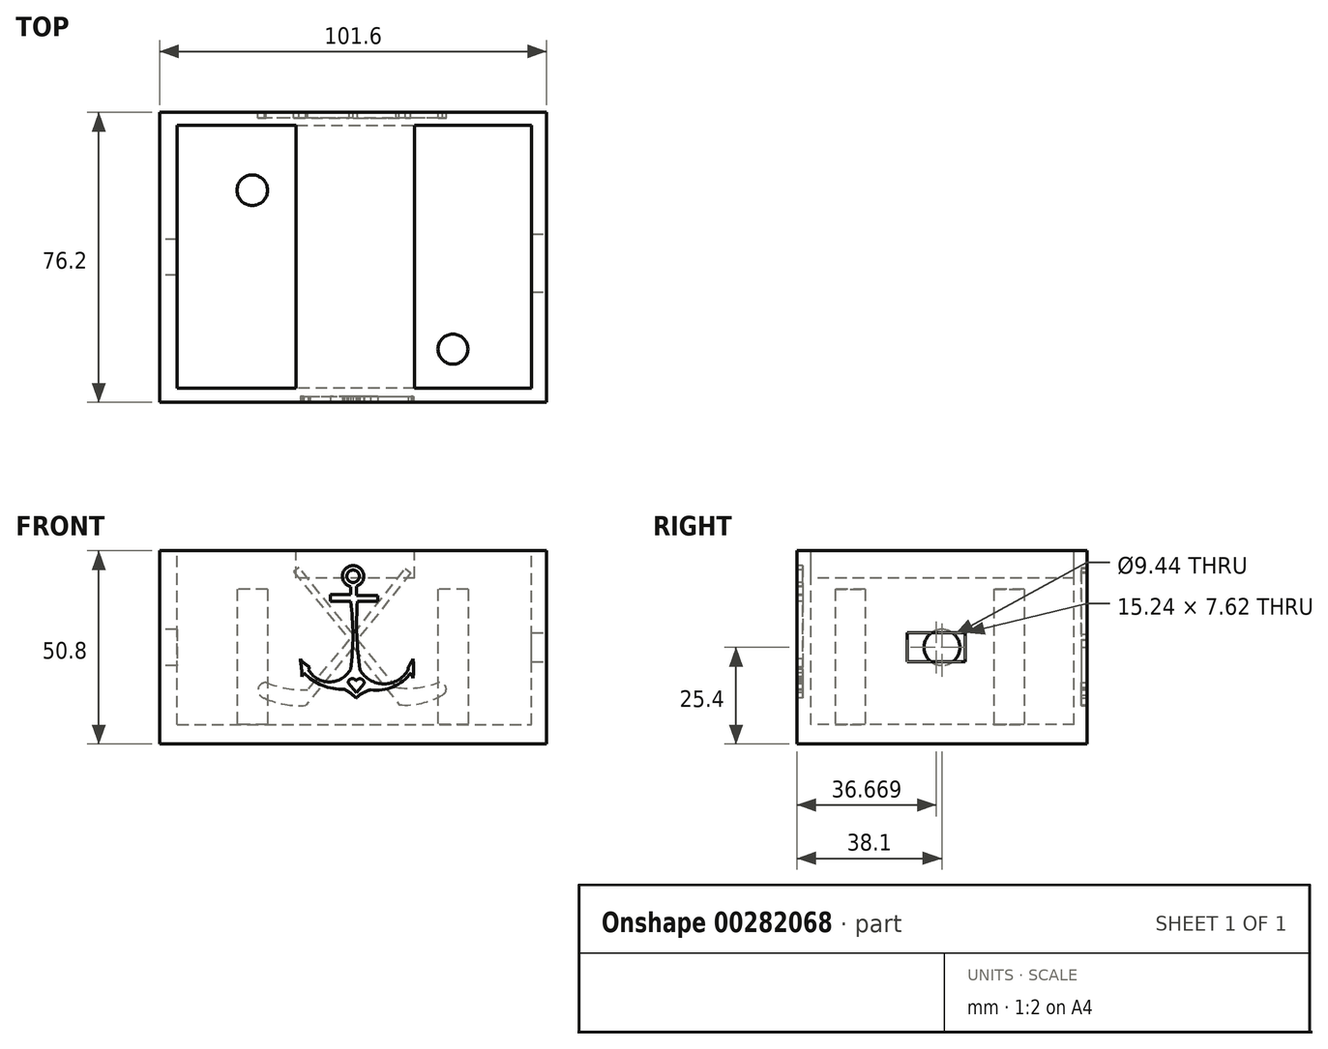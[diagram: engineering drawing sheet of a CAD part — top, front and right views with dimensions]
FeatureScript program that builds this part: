
annotation { "Feature Type Name" : "Feature", "Feature Type Description" : "" }
export const myFeature = defineFeature(function(context is Context, id is Id, definition is map)
    precondition{}
    {
        {
            var Q0;
            Q0=qCreatedBy(makeId("Front.planeOp"),FACE);
            var sketch = newSketch(context, id + "F0", { "sketchPlane" : qUnion([Q0])});
            skLineSegment(sketch, "E0.bottom", {"start": v(-50.8, 25.4) * mm, "end": v(50.8, 25.4) * mm});
            skLineSegment(sketch, "E0.top", {"start": v(-50.8, -25.4) * mm, "end": v(50.8, -25.4) * mm});
            skLineSegment(sketch, "E0.left", {"start": v(-50.8, 25.4) * mm, "end": v(-50.8, -25.4) * mm});
            skLineSegment(sketch, "E0.right", {"start": v(50.8, 25.4) * mm, "end": v(50.8, -25.4) * mm});
            skPoint(sketch, "E0.middle", {"position": v(0, 0) * mm});
            skSolve(sketch);
        }
        {
            var Q0;
            Q0=makeQuery(id+"F0.imprint","IMPRINT",FACE,{"disambiguationData":[TD([[makeQuery(id+"F0.imprint","IMPRINT",EDGE,{"derivedFrom":sQuery(id+"F0.wireOp",EDGE,"E0.bottom")}),-1.0]])]});
            extrude(context, id + "F1", {"entities" : qUnion([Q0]), "oppositeDirection" : true, "depth" : 76.2 * mm});
        }
        {
            var Q0;
            Q0=makeQuery(id+"F1.opExtrude","SWEPT_FACE",FACE,{"disambiguationData":[OSD([sQuery(id+"F0.wireOp",EDGE,"E0.bottom")])]});
            var sketch = newSketch(context, id + "F2", { "sketchPlane" : qUnion([Q0])});
            skLineSegment(sketch, "E1.bottom", {"start": v(-46.23, 72.86) * mm, "end": v(-14.92, 72.86) * mm});
            skLineSegment(sketch, "E1.top", {"start": v(-46.23, 3.7) * mm, "end": v(-14.92, 3.7) * mm});
            skLineSegment(sketch, "E1.left", {"start": v(-46.23, 72.86) * mm, "end": v(-46.23, 3.7) * mm});
            skLineSegment(sketch, "E1.right", {"start": v(46.93, 72.86) * mm, "end": v(46.93, 3.7) * mm});
            skLineSegment(sketch, "E2.bottom", {"start": v(16.2, 76.2) * mm, "end": v(-14.92, 76.2) * mm});
            skLineSegment(sketch, "E2.top", {"start": v(16.2, 0) * mm, "end": v(-14.92, 0) * mm});
            skLineSegment(sketch, "E2.left", {"start": v(16.2, 76.2) * mm, "end": v(16.2, 0) * mm});
            skLineSegment(sketch, "E2.right", {"start": v(-14.92, 76.2) * mm, "end": v(-14.92, 0) * mm});
            skLineSegment(sketch, "E3.trimOffspring", {"start": v(16.2, 72.86) * mm, "end": v(46.93, 72.86) * mm});
            skLineSegment(sketch, "E4.trimOffspring", {"start": v(16.2, 3.7) * mm, "end": v(46.93, 3.7) * mm});
            skSolve(sketch);
        }
        {
            var Q0;
            {var subQ0=sQuery(id+"F2.wireOp",EDGE,"E1.bottom");Q0=makeQuery(id+"F2.imprint","IMPRINT",FACE,{"disambiguationData":[TD([[makeQuery(id+"F2.imprint","IMPRINT",EDGE,{"derivedFrom":subQ0}),-1.0]])]});}
            var Q1;
            Q1=makeQuery(id+"F2.imprint","IMPRINT",FACE,{"disambiguationData":[TD([[makeQuery(id+"F2.imprint","IMPRINT",EDGE,{"derivedFrom":sQuery(id+"F2.wireOp",EDGE,"E1.right")}),-1.0]])]});
            extrude(context, id + "F3", {"entities" : qUnion([Q0, Q1]), "operationType" : NewBodyOperationType.REMOVE, "oppositeDirection" : true, "depth" : 45.72 * mm});
        }
        {
            var Q0;
            Q0=makeQuery(id+"F3.boolean.opBoolean","COPY",FACE,{"derivedFrom":makeQuery(id+"F3.opExtrude","SWEPT_FACE",FACE,{"disambiguationData":[OSD([sQuery(id+"F2.wireOp",EDGE,"E2.right")])]})});
            var sketch = newSketch(context, id + "F4", { "sketchPlane" : qUnion([Q0])});
            skLineSegment(sketch, "E5.bottom", {"start": v(-72.86, 18.27) * mm, "end": v(-3.7, 18.27) * mm});
            skLineSegment(sketch, "E5.top", {"start": v(-72.86, -20.32) * mm, "end": v(-3.7, -20.32) * mm});
            skLineSegment(sketch, "E5.left", {"start": v(-72.86, 18.27) * mm, "end": v(-72.86, -20.32) * mm});
            skLineSegment(sketch, "E5.right", {"start": v(-3.7, 18.27) * mm, "end": v(-3.7, -20.32) * mm});
            skSolve(sketch);
        }
        {
            var Q0;
            Q0 = qSketchRegion(id + "F4", true);
            extrude(context, id + "F5", {"entities" : qUnion([Q0]), "operationType" : NewBodyOperationType.REMOVE, "oppositeDirection" : true, "depth" : 50.8 * mm});
        }
        {
            var Q0;
            Q0=makeQuery(id+"F1.opExtrude","SWEPT_FACE",FACE,{"disambiguationData":[OSD([sQuery(id+"F0.wireOp",EDGE,"E0.right")])]});
            var sketch = newSketch(context, id + "F6", { "sketchPlane" : qUnion([Q0])});
            skLineSegment(sketch, "E6.bottom", {"start": v(29.05, 3.81) * mm, "end": v(44.29, 3.81) * mm});
            skLineSegment(sketch, "E6.top", {"start": v(29.05, -3.81) * mm, "end": v(44.29, -3.81) * mm});
            skLineSegment(sketch, "E6.left", {"start": v(29.05, 3.81) * mm, "end": v(29.05, -3.81) * mm});
            skLineSegment(sketch, "E6.right", {"start": v(44.29, 3.81) * mm, "end": v(44.29, -3.81) * mm});
            skSolve(sketch);
        }
        {
            var Q0;
            Q0=makeQuery(id+"F6.imprint","IMPRINT",FACE,{"disambiguationData":[TD([[makeQuery(id+"F6.imprint","IMPRINT",EDGE,{"derivedFrom":sQuery(id+"F6.wireOp",EDGE,"E6.bottom")}),-1.0]])]});
            extrude(context, id + "F7", {"entities" : qUnion([Q0]), "operationType" : NewBodyOperationType.REMOVE, "oppositeDirection" : true, "depth" : 10.16 * mm});
        }
        {
            var Q0;
            Q0=makeQuery(id+"F1.opExtrude","SWEPT_FACE",FACE,{"disambiguationData":[OSD([sQuery(id+"F0.wireOp",EDGE,"E0.left")])]});
            var sketch = newSketch(context, id + "F8", { "sketchPlane" : qUnion([Q0])});
            skCircle(sketch, "E7", {"center": v(-38.1, 0) * mm, "radius": 4.72 * mm});
            skPoint(sketch, "E7.centerSnap0", {"position": v(-38.1, 25.4) * mm});
            skSolve(sketch);
        }
        {
            var Q0;
            Q0=makeQuery(id+"F8.imprint","IMPRINT",FACE,{"disambiguationData":[TD([[makeQuery(id+"F8.imprint","IMPRINT",EDGE,{"derivedFrom":sQuery(id+"F8.wireOp",EDGE,"E7")}),1.0]])]});
            extrude(context, id + "F9", {"entities" : qUnion([Q0]), "operationType" : NewBodyOperationType.REMOVE, "oppositeDirection" : true, "depth" : 12.7 * mm});
        }
        {
            var Q0;
            Q0=makeQuery(id+"F1.opExtrude","CAP_FACE",FACE,{"disambiguationData":[OSD([sQuery(id+"F0.wireOp",EDGE,"E0.bottom"),sQuery(id+"F0.wireOp",EDGE,"E0.top"),sQuery(id+"F0.wireOp",EDGE,"E0.left"),sQuery(id+"F0.wireOp",EDGE,"E0.right")])],"isStart":true});
            var sketch = newSketch(context, id + "F10", { "sketchPlane" : qUnion([Q0])});
            skCircle(sketch, "E8", {"center": v(0, 18.69) * mm, "radius": 2.8 * mm});
            skCircle(sketch, "E9", {"center": v(0, 18.69) * mm, "radius": 1.64 * mm});
            skLineSegment(sketch, "E10", {"start": v(-0.66, 15.97) * mm, "end": v(-0.66, 13.82) * mm});
            skLineSegment(sketch, "E11", {"start": v(-5.92, 12.1) * mm, "end": v(-0.66, 12.1) * mm});
            skLineSegment(sketch, "E12", {"start": v(0.87, 16.03) * mm, "end": v(0.87, 13.68) * mm});
            skLineSegment(sketch, "E13", {"start": v(0.87, 13.68) * mm, "end": v(6.55, 13.68) * mm});
            skLineSegment(sketch, "E14", {"start": v(6.55, 13.68) * mm, "end": v(6.55, 12.14) * mm});
            skLineSegment(sketch, "E15", {"start": v(6.55, 12.14) * mm, "end": v(1.13, 12.14) * mm});
            skLineSegment(sketch, "E16", {"start": v(-0.66, 13.82) * mm, "end": v(-5.92, 13.82) * mm});
            skLineSegment(sketch, "E17", {"start": v(-5.92, 13.82) * mm, "end": v(-5.92, 12.1) * mm});
            skArc(sketch, "E18", {"start": v(-0.66, -5.74) * mm, "mid": v(-0.03, 3.18) * mm, "end": v(-0.66, 12.1) * mm});
            skArc(sketch, "E19", {"start": v(1.13, 12.14) * mm, "mid": v(1, 3.13) * mm, "end": v(1.81, -5.85) * mm});
            skArc(sketch, "E20", {"start": v(1.81, -5.85) * mm, "mid": v(8.13, -9.59) * mm, "end": v(14.45, -5.85) * mm});
            skArc(sketch, "E21", {"start": v(-11.77, -5.74) * mm, "mid": v(-6.22, -9.08) * mm, "end": v(-0.66, -5.74) * mm});
            skArc(sketch, "E22", {"start": v(-13.88, -3.06) * mm, "mid": v(-12.7, -4.3) * mm, "end": v(-11.25, -5.22) * mm});
            skArc(sketch, "E23", {"start": v(-13.4, -7.74) * mm, "mid": v(-13.56, -5.4) * mm, "end": v(-13.88, -3.06) * mm});
            skArc(sketch, "E24", {"start": v(14.45, -5.32) * mm, "mid": v(15.1, -4.2) * mm, "end": v(15.72, -3.06) * mm});
            skArc(sketch, "E25", {"start": v(15.72, -8.11) * mm, "mid": v(15.93, -5.58) * mm, "end": v(15.72, -3.06) * mm});
            skArc(sketch, "E26", {"start": v(-12.93, -6.74) * mm, "mid": v(-8.05, -9.97) * mm, "end": v(-2.3, -11.06) * mm});
            skArc(sketch, "E27", {"start": v(4.55, -11.17) * mm, "mid": v(10.5, -10.35) * mm, "end": v(15.24, -6.64) * mm});
            skArc(sketch, "E28", {"start": v(0.81, -13.33) * mm, "mid": v(-0.64, -12.05) * mm, "end": v(-2.3, -11.06) * mm});
            skArc(sketch, "E29", {"start": v(4.55, -11.17) * mm, "mid": v(2.52, -11.97) * mm, "end": v(0.81, -13.33) * mm});
            skArc(sketch, "E30", {"start": v(2.92, -9.43) * mm, "mid": v(2.13, -8.29) * mm, "end": v(0.81, -8.74) * mm});
            skArc(sketch, "E31", {"start": v(0.81, -8.74) * mm, "mid": v(-0.46, -8.24) * mm, "end": v(-1.3, -9.32) * mm});
            skLineSegment(sketch, "E32", {"start": v(2.92, -9.43) * mm, "end": v(0.86, -11.96) * mm});
            skLineSegment(sketch, "E33", {"start": v(0.86, -11.96) * mm, "end": v(-1.3, -9.32) * mm});
            skLineSegment(sketch, "E34", {"start": v(-11.77, -5.74) * mm, "end": v(-11.25, -5.22) * mm});
            skLineSegment(sketch, "E35", {"start": v(-12.93, -6.74) * mm, "end": v(-13.4, -7.74) * mm});
            skLineSegment(sketch, "E36", {"start": v(15.72, -8.11) * mm, "end": v(15.24, -6.64) * mm});
            skLineSegment(sketch, "E37", {"start": v(14.45, -5.85) * mm, "end": v(14.45, -5.32) * mm});
            skSolve(sketch);
        }
        {
            var Q0;
            Q0 = qSketchRegion(id + "F10", true);
            extrude(context, id + "F11", {"entities" : qUnion([Q0]), "operationType" : NewBodyOperationType.REMOVE, "oppositeDirection" : true, "depth" : 1.52 * mm});
        }
        {
            var Q0;
            Q0=makeQuery(id+"F1.opExtrude","CAP_FACE",FACE,{"disambiguationData":[OSD([sQuery(id+"F0.wireOp",EDGE,"E0.bottom"),sQuery(id+"F0.wireOp",EDGE,"E0.top"),sQuery(id+"F0.wireOp",EDGE,"E0.left"),sQuery(id+"F0.wireOp",EDGE,"E0.right")])],"isStart":false});
            var sketch = newSketch(context, id + "F12", { "sketchPlane" : qUnion([Q0])});
            skLineSegment(sketch, "E38", {"start": v(0, 3.47) * mm, "end": v(14.23, 20.98) * mm});
            skLineSegment(sketch, "E39", {"start": v(14.23, 20.98) * mm, "end": v(15.57, 19.9) * mm});
            skLineSegment(sketch, "E40", {"start": v(15.57, 19.9) * mm, "end": v(1.04, 2.03) * mm});
            skLineSegment(sketch, "E41", {"start": v(1.04, 2.03) * mm, "end": v(11.95, -11.13) * mm});
            skLineSegment(sketch, "E42", {"start": v(0, 3.47) * mm, "end": v(-13.78, 20.75) * mm});
            skLineSegment(sketch, "E43", {"start": v(-13.78, 20.75) * mm, "end": v(-15.17, 19.63) * mm});
            skLineSegment(sketch, "E44", {"start": v(-15.17, 19.63) * mm, "end": v(-1.12, 2) * mm});
            skLineSegment(sketch, "E45", {"start": v(-1.12, 2) * mm, "end": v(-11.3, -10.51) * mm});
            skLineSegment(sketch, "E46", {"start": v(0, 0) * mm, "end": v(-12.12, -15.08) * mm});
            skLineSegment(sketch, "E47", {"start": v(0, 0) * mm, "end": v(12.42, -15.23) * mm});
            skArc(sketch, "E48", {"start": v(-22.38, -9.24) * mm, "mid": v(-16.92, -10.62) * mm, "end": v(-11.3, -10.51) * mm});
            skArc(sketch, "E49", {"start": v(-23.48, -12.47) * mm, "mid": v(-18, -14.68) * mm, "end": v(-12.12, -15.08) * mm});
            skArc(sketch, "E50", {"start": v(-22.38, -9.24) * mm, "mid": v(-24.38, -10.36) * mm, "end": v(-23.48, -12.47) * mm});
            skArc(sketch, "E51", {"start": v(11.95, -11.13) * mm, "mid": v(17.5, -10.8) * mm, "end": v(22.84, -9.24) * mm});
            skArc(sketch, "E52", {"start": v(12.42, -15.23) * mm, "mid": v(17.94, -14.97) * mm, "end": v(23.23, -13.34) * mm});
            skArc(sketch, "E53", {"start": v(23.23, -13.34) * mm, "mid": v(24.97, -11.1) * mm, "end": v(22.84, -9.24) * mm});
            skSolve(sketch);
        }
        {
            var Q0;
            Q0 = qSketchRegion(id + "F12", true);
            extrude(context, id + "F13", {"entities" : qUnion([Q0]), "operationType" : NewBodyOperationType.REMOVE, "oppositeDirection" : true, "depth" : 1.52 * mm});
        }
        {
            var Q0;
            Q0=makeQuery(id+"F5.boolean.opBoolean","MERGE",FACE,{"derivedFrom":[makeQuery(id+"F3.boolean.opBoolean","COPY",FACE,{"derivedFrom":makeQuery(id+"F3.opExtrude","CAP_FACE",FACE,{"disambiguationData":[OSD([sQuery(id+"F2.wireOp",EDGE,"E1.bottom"),sQuery(id+"F2.wireOp",EDGE,"E1.top"),sQuery(id+"F2.wireOp",EDGE,"E1.left"),sQuery(id+"F2.wireOp",EDGE,"E2.right")])],"isStart":false})}),makeQuery(id+"F3.boolean.opBoolean","COPY",FACE,{"derivedFrom":makeQuery(id+"F3.opExtrude","CAP_FACE",FACE,{"disambiguationData":[OSD([sQuery(id+"F2.wireOp",EDGE,"E1.right"),sQuery(id+"F2.wireOp",EDGE,"E2.left"),sQuery(id+"F2.wireOp",EDGE,"E3.trimOffspring"),sQuery(id+"F2.wireOp",EDGE,"E4.trimOffspring")])],"isStart":false})}),makeQuery(id+"F5.opExtrude","SWEPT_FACE",FACE,{"disambiguationData":[OSD([sQuery(id+"F4.wireOp",EDGE,"E5.top")])]})]});
            var sketch = newSketch(context, id + "F14", { "sketchPlane" : qUnion([Q0])});
            skCircle(sketch, "E54", {"center": v(-26.48, 55.73) * mm, "radius": 4 * mm});
            skCircle(sketch, "E55", {"center": v(26.23, 13.98) * mm, "radius": 3.94 * mm});
            skSolve(sketch);
        }
        {
            var Q0;
            Q0 = qSketchRegion(id + "F14", true);
            extrude(context, id + "F15", {"entities" : qUnion([Q0]), "operationType" : NewBodyOperationType.ADD, "depth" : 35.56 * mm});
        }
    });
